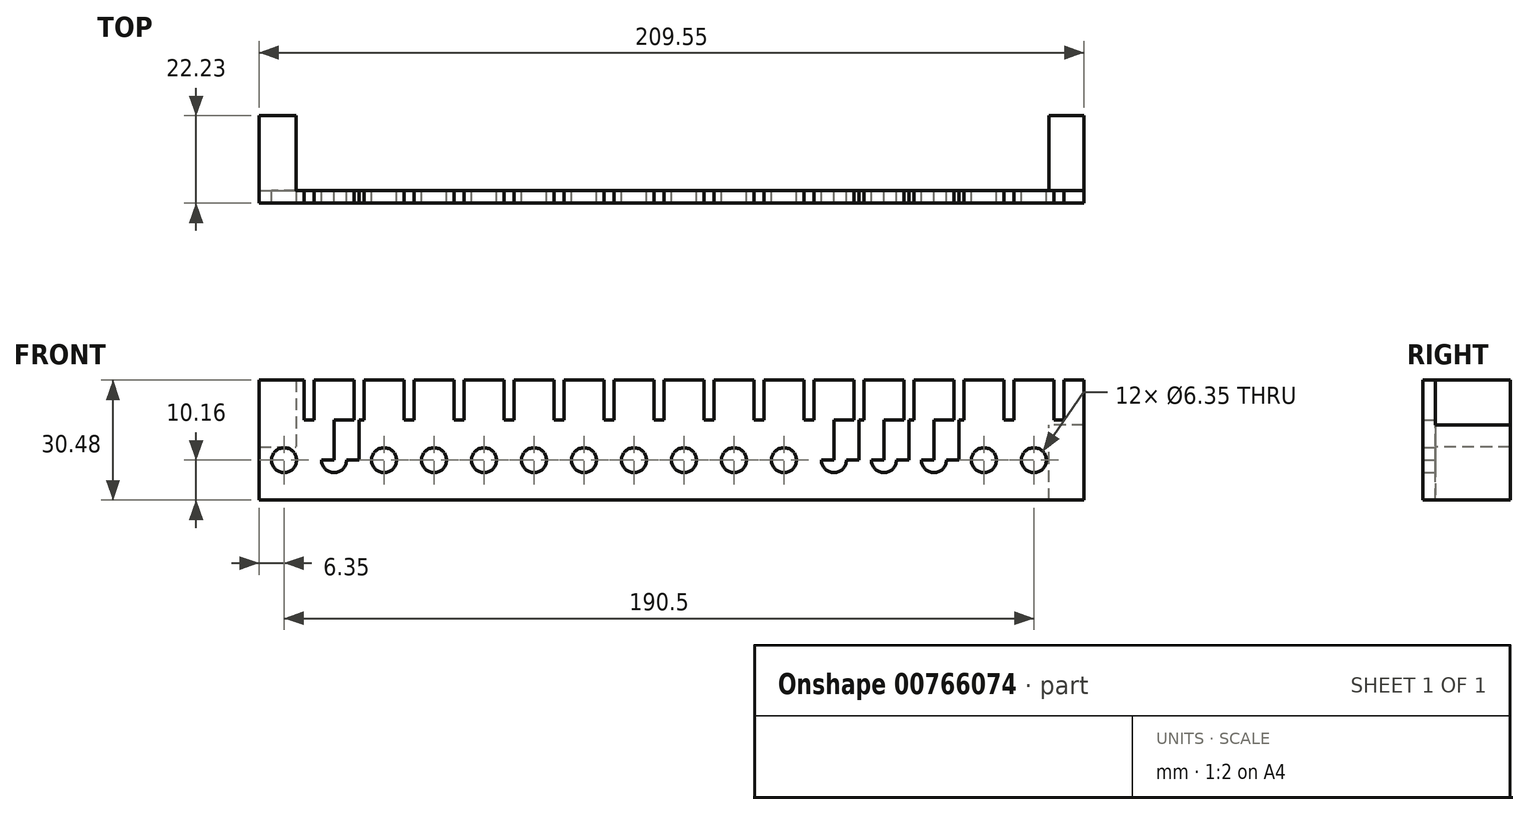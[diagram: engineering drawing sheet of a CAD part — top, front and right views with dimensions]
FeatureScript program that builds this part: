
annotation { "Feature Type Name" : "Feature", "Feature Type Description" : "" }
export const myFeature = defineFeature(function(context is Context, id is Id, definition is map)
    precondition{}
    {
        {
            var Q0;
            Q0=qCreatedBy(makeId("Front.planeOp"),FACE);
            var sketch = newSketch(context, id + "F0", { "sketchPlane" : qUnion([Q0])});
            skLineSegment(sketch, "E0.bottom", {"start": v(-95.25, 15.24) * mm, "end": v(95.25, 15.24) * mm});
            skLineSegment(sketch, "E0.top", {"start": v(-95.25, -15.24) * mm, "end": v(95.25, -15.24) * mm});
            skLineSegment(sketch, "E0.left", {"start": v(-95.25, 15.24) * mm, "end": v(-95.25, -15.24) * mm});
            skLineSegment(sketch, "E0.right", {"start": v(95.25, 15.24) * mm, "end": v(95.25, -15.24) * mm});
            skPoint(sketch, "E0.middle", {"position": v(0, 0) * mm});
            skLineSegment(sketch, "E1", {"start": v(-95.25, -5.08) * mm, "end": v(95.25, -5.08) * mm});
            skLineSegment(sketch, "E2", {"start": v(-95.25, 5.08) * mm, "end": v(95.25, 5.08) * mm});
            skLineSegment(sketch, "E3", {"start": v(-88.9, 15.24) * mm, "end": v(-88.9, -15.24) * mm});
            skLineSegment(sketch, "E4", {"start": v(-76.2, 15.24) * mm, "end": v(-76.2, -15.24) * mm});
            skLineSegment(sketch, "E5", {"start": v(-82.55, 15.24) * mm, "end": v(-82.55, -15.24) * mm});
            skLineSegment(sketch, "E6", {"start": v(-69.85, 15.24) * mm, "end": v(-69.85, -15.24) * mm});
            skLineSegment(sketch, "E7.bottom", {"start": v(-81.28, 5.08) * mm, "end": v(-83.82, 5.08) * mm});
            skLineSegment(sketch, "E7.top", {"start": v(-81.28, 25.4) * mm, "end": v(-83.82, 25.4) * mm});
            skLineSegment(sketch, "E7.left", {"start": v(-81.28, 5.08) * mm, "end": v(-81.28, 25.4) * mm});
            skLineSegment(sketch, "E7.right", {"start": v(-83.82, 5.08) * mm, "end": v(-83.82, 25.4) * mm});
            skPoint(sketch, "E7.middle", {"position": v(-82.55, 15.24) * mm});
            skLineSegment(sketch, "E8.bottom", {"start": v(-68.58, 5.08) * mm, "end": v(-71.12, 5.08) * mm});
            skLineSegment(sketch, "E8.top", {"start": v(-68.58, 25.4) * mm, "end": v(-71.12, 25.4) * mm});
            skLineSegment(sketch, "E8.left", {"start": v(-68.58, 5.08) * mm, "end": v(-68.58, 25.4) * mm});
            skLineSegment(sketch, "E8.right", {"start": v(-71.12, 5.08) * mm, "end": v(-71.12, 25.4) * mm});
            skPoint(sketch, "E8.middle", {"position": v(-69.85, 15.24) * mm});
            skCircle(sketch, "E9", {"center": v(-88.9, -5.08) * mm, "radius": 3.18 * mm});
            skCircle(sketch, "E10", {"center": v(-76.2, -5.08) * mm, "radius": 3.18 * mm});
            skLineSegment(sketch, "E11", {"start": v(-63.5, 15.24) * mm, "end": v(-63.5, -15.24) * mm});
            skLineSegment(sketch, "E12", {"start": v(-50.8, 15.24) * mm, "end": v(-50.8, -15.24) * mm});
            skLineSegment(sketch, "E13", {"start": v(-57.15, 15.24) * mm, "end": v(-57.15, -15.24) * mm});
            skLineSegment(sketch, "E14", {"start": v(-44.45, 15.24) * mm, "end": v(-44.45, -15.24) * mm});
            skLineSegment(sketch, "E15.bottom", {"start": v(-55.88, 5.08) * mm, "end": v(-58.42, 5.08) * mm});
            skLineSegment(sketch, "E15.top", {"start": v(-55.88, 25.4) * mm, "end": v(-58.42, 25.4) * mm});
            skLineSegment(sketch, "E15.left", {"start": v(-55.88, 5.08) * mm, "end": v(-55.88, 25.4) * mm});
            skLineSegment(sketch, "E15.right", {"start": v(-58.42, 5.08) * mm, "end": v(-58.42, 25.4) * mm});
            skPoint(sketch, "E15.middle", {"position": v(-57.15, 15.24) * mm});
            skLineSegment(sketch, "E16.bottom", {"start": v(-43.18, 5.08) * mm, "end": v(-45.72, 5.08) * mm});
            skLineSegment(sketch, "E16.top", {"start": v(-43.18, 25.4) * mm, "end": v(-45.72, 25.4) * mm});
            skLineSegment(sketch, "E16.left", {"start": v(-43.18, 5.08) * mm, "end": v(-43.18, 25.4) * mm});
            skLineSegment(sketch, "E16.right", {"start": v(-45.72, 5.08) * mm, "end": v(-45.72, 25.4) * mm});
            skPoint(sketch, "E16.middle", {"position": v(-44.45, 15.24) * mm});
            skCircle(sketch, "E17", {"center": v(-63.5, -5.08) * mm, "radius": 3.18 * mm});
            skCircle(sketch, "E18", {"center": v(-50.8, -5.08) * mm, "radius": 3.18 * mm});
            skLineSegment(sketch, "E19", {"start": v(-38.1, 15.24) * mm, "end": v(-38.1, -15.24) * mm});
            skLineSegment(sketch, "E20", {"start": v(-25.4, 15.24) * mm, "end": v(-25.4, -15.24) * mm});
            skLineSegment(sketch, "E21", {"start": v(-31.75, 15.24) * mm, "end": v(-31.75, -15.24) * mm});
            skLineSegment(sketch, "E22", {"start": v(-19.05, 15.24) * mm, "end": v(-19.05, -15.24) * mm});
            skLineSegment(sketch, "E23.bottom", {"start": v(-30.48, 5.08) * mm, "end": v(-33.02, 5.08) * mm});
            skLineSegment(sketch, "E23.top", {"start": v(-30.48, 25.4) * mm, "end": v(-33.02, 25.4) * mm});
            skLineSegment(sketch, "E23.left", {"start": v(-30.48, 5.08) * mm, "end": v(-30.48, 25.4) * mm});
            skLineSegment(sketch, "E23.right", {"start": v(-33.02, 5.08) * mm, "end": v(-33.02, 25.4) * mm});
            skPoint(sketch, "E23.middle", {"position": v(-31.75, 15.24) * mm});
            skLineSegment(sketch, "E24.bottom", {"start": v(-17.78, 5.08) * mm, "end": v(-20.32, 5.08) * mm});
            skLineSegment(sketch, "E24.top", {"start": v(-17.78, 25.4) * mm, "end": v(-20.32, 25.4) * mm});
            skLineSegment(sketch, "E24.left", {"start": v(-17.78, 5.08) * mm, "end": v(-17.78, 25.4) * mm});
            skLineSegment(sketch, "E24.right", {"start": v(-20.32, 5.08) * mm, "end": v(-20.32, 25.4) * mm});
            skPoint(sketch, "E24.middle", {"position": v(-19.05, 15.24) * mm});
            skCircle(sketch, "E25", {"center": v(-38.1, -5.08) * mm, "radius": 3.18 * mm});
            skCircle(sketch, "E26", {"center": v(-25.4, -5.08) * mm, "radius": 3.18 * mm});
            skLineSegment(sketch, "E27", {"start": v(-12.7, 15.24) * mm, "end": v(-12.7, -15.24) * mm});
            skLineSegment(sketch, "E28", {"start": v(0, 15.24) * mm, "end": v(0, -15.24) * mm});
            skLineSegment(sketch, "E29", {"start": v(-6.35, 15.24) * mm, "end": v(-6.35, -15.24) * mm});
            skLineSegment(sketch, "E30", {"start": v(6.35, 15.24) * mm, "end": v(6.35, -15.24) * mm});
            skLineSegment(sketch, "E31.bottom", {"start": v(-5.08, 5.08) * mm, "end": v(-7.62, 5.08) * mm});
            skLineSegment(sketch, "E31.top", {"start": v(-5.08, 25.4) * mm, "end": v(-7.62, 25.4) * mm});
            skLineSegment(sketch, "E31.left", {"start": v(-5.08, 5.08) * mm, "end": v(-5.08, 25.4) * mm});
            skLineSegment(sketch, "E31.right", {"start": v(-7.62, 5.08) * mm, "end": v(-7.62, 25.4) * mm});
            skPoint(sketch, "E31.middle", {"position": v(-6.35, 15.24) * mm});
            skLineSegment(sketch, "E32.bottom", {"start": v(7.62, 5.08) * mm, "end": v(5.08, 5.08) * mm});
            skLineSegment(sketch, "E32.top", {"start": v(7.62, 25.4) * mm, "end": v(5.08, 25.4) * mm});
            skLineSegment(sketch, "E32.left", {"start": v(7.62, 5.08) * mm, "end": v(7.62, 25.4) * mm});
            skLineSegment(sketch, "E32.right", {"start": v(5.08, 5.08) * mm, "end": v(5.08, 25.4) * mm});
            skPoint(sketch, "E32.middle", {"position": v(6.35, 15.24) * mm});
            skCircle(sketch, "E33", {"center": v(-12.7, -5.08) * mm, "radius": 3.18 * mm});
            skCircle(sketch, "E34", {"center": v(0, -5.08) * mm, "radius": 3.18 * mm});
            skLineSegment(sketch, "E35", {"start": v(12.7, 15.24) * mm, "end": v(12.7, -15.24) * mm});
            skLineSegment(sketch, "E36", {"start": v(25.4, 15.24) * mm, "end": v(25.4, -15.24) * mm});
            skLineSegment(sketch, "E37", {"start": v(19.05, 15.24) * mm, "end": v(19.05, -15.24) * mm});
            skLineSegment(sketch, "E38", {"start": v(31.75, 15.24) * mm, "end": v(31.75, -15.24) * mm});
            skLineSegment(sketch, "E39.bottom", {"start": v(20.32, 5.08) * mm, "end": v(17.78, 5.08) * mm});
            skLineSegment(sketch, "E39.top", {"start": v(20.32, 25.4) * mm, "end": v(17.78, 25.4) * mm});
            skLineSegment(sketch, "E39.left", {"start": v(20.32, 5.08) * mm, "end": v(20.32, 25.4) * mm});
            skLineSegment(sketch, "E39.right", {"start": v(17.78, 5.08) * mm, "end": v(17.78, 25.4) * mm});
            skPoint(sketch, "E39.middle", {"position": v(19.05, 15.24) * mm});
            skLineSegment(sketch, "E40.bottom", {"start": v(33.02, 5.08) * mm, "end": v(30.48, 5.08) * mm});
            skLineSegment(sketch, "E40.top", {"start": v(33.02, 25.4) * mm, "end": v(30.48, 25.4) * mm});
            skLineSegment(sketch, "E40.left", {"start": v(33.02, 5.08) * mm, "end": v(33.02, 25.4) * mm});
            skLineSegment(sketch, "E40.right", {"start": v(30.48, 5.08) * mm, "end": v(30.48, 25.4) * mm});
            skPoint(sketch, "E40.middle", {"position": v(31.75, 15.24) * mm});
            skCircle(sketch, "E41", {"center": v(12.7, -5.08) * mm, "radius": 3.18 * mm});
            skCircle(sketch, "E42", {"center": v(25.4, -5.08) * mm, "radius": 3.18 * mm});
            skLineSegment(sketch, "E43", {"start": v(38.1, 15.24) * mm, "end": v(38.1, -15.24) * mm});
            skLineSegment(sketch, "E44", {"start": v(50.8, 15.24) * mm, "end": v(50.8, -15.24) * mm});
            skLineSegment(sketch, "E45", {"start": v(44.45, 15.24) * mm, "end": v(44.45, -15.24) * mm});
            skLineSegment(sketch, "E46", {"start": v(57.15, 15.24) * mm, "end": v(57.15, -15.24) * mm});
            skLineSegment(sketch, "E47.bottom", {"start": v(45.72, 5.08) * mm, "end": v(43.18, 5.08) * mm});
            skLineSegment(sketch, "E47.top", {"start": v(45.72, 25.4) * mm, "end": v(43.18, 25.4) * mm});
            skLineSegment(sketch, "E47.left", {"start": v(45.72, 5.08) * mm, "end": v(45.72, 25.4) * mm});
            skLineSegment(sketch, "E47.right", {"start": v(43.18, 5.08) * mm, "end": v(43.18, 25.4) * mm});
            skPoint(sketch, "E47.middle", {"position": v(44.45, 15.24) * mm});
            skLineSegment(sketch, "E48.bottom", {"start": v(58.42, 5.08) * mm, "end": v(55.88, 5.08) * mm});
            skLineSegment(sketch, "E48.top", {"start": v(58.42, 25.4) * mm, "end": v(55.88, 25.4) * mm});
            skLineSegment(sketch, "E48.left", {"start": v(58.42, 5.08) * mm, "end": v(58.42, 25.4) * mm});
            skLineSegment(sketch, "E48.right", {"start": v(55.88, 5.08) * mm, "end": v(55.88, 25.4) * mm});
            skPoint(sketch, "E48.middle", {"position": v(57.15, 15.24) * mm});
            skCircle(sketch, "E49", {"center": v(38.1, -5.08) * mm, "radius": 3.18 * mm});
            skCircle(sketch, "E50", {"center": v(50.8, -5.08) * mm, "radius": 3.18 * mm});
            skLineSegment(sketch, "E51", {"start": v(63.5, 15.24) * mm, "end": v(63.5, -15.24) * mm});
            skLineSegment(sketch, "E52", {"start": v(76.2, 15.24) * mm, "end": v(76.2, -15.24) * mm});
            skLineSegment(sketch, "E53", {"start": v(69.85, 15.24) * mm, "end": v(69.85, -15.24) * mm});
            skLineSegment(sketch, "E54", {"start": v(82.55, 15.24) * mm, "end": v(82.55, -15.24) * mm});
            skLineSegment(sketch, "E55.bottom", {"start": v(71.12, 5.08) * mm, "end": v(68.58, 5.08) * mm});
            skLineSegment(sketch, "E55.top", {"start": v(71.12, 25.4) * mm, "end": v(68.58, 25.4) * mm});
            skLineSegment(sketch, "E55.left", {"start": v(71.12, 5.08) * mm, "end": v(71.12, 25.4) * mm});
            skLineSegment(sketch, "E55.right", {"start": v(68.58, 5.08) * mm, "end": v(68.58, 25.4) * mm});
            skPoint(sketch, "E55.middle", {"position": v(69.85, 15.24) * mm});
            skLineSegment(sketch, "E56.bottom", {"start": v(83.82, 5.08) * mm, "end": v(81.28, 5.08) * mm});
            skLineSegment(sketch, "E56.top", {"start": v(83.82, 25.4) * mm, "end": v(81.28, 25.4) * mm});
            skLineSegment(sketch, "E56.left", {"start": v(83.82, 5.08) * mm, "end": v(83.82, 25.4) * mm});
            skLineSegment(sketch, "E56.right", {"start": v(81.28, 5.08) * mm, "end": v(81.28, 25.4) * mm});
            skPoint(sketch, "E56.middle", {"position": v(82.55, 15.24) * mm});
            skCircle(sketch, "E57", {"center": v(63.5, -5.08) * mm, "radius": 3.18 * mm});
            skCircle(sketch, "E58", {"center": v(76.2, -5.08) * mm, "radius": 3.18 * mm});
            skLineSegment(sketch, "E59", {"start": v(88.9, 15.24) * mm, "end": v(88.9, -15.24) * mm});
            skLineSegment(sketch, "E60", {"start": v(101.6, 15.24) * mm, "end": v(101.6, -15.24) * mm});
            skLineSegment(sketch, "E61", {"start": v(107.95, 15.24) * mm, "end": v(107.95, -15.24) * mm});
            skLineSegment(sketch, "E62.bottom", {"start": v(96.52, 5.08) * mm, "end": v(93.98, 5.08) * mm});
            skLineSegment(sketch, "E62.top", {"start": v(96.52, 25.4) * mm, "end": v(93.98, 25.4) * mm});
            skLineSegment(sketch, "E62.left", {"start": v(96.52, 5.08) * mm, "end": v(96.52, 25.4) * mm});
            skLineSegment(sketch, "E62.right", {"start": v(93.98, 5.08) * mm, "end": v(93.98, 25.4) * mm});
            skPoint(sketch, "E62.middle", {"position": v(95.25, 15.24) * mm});
            skLineSegment(sketch, "E63.bottom", {"start": v(109.22, 5.08) * mm, "end": v(106.68, 5.08) * mm});
            skLineSegment(sketch, "E63.top", {"start": v(109.22, 25.4) * mm, "end": v(106.68, 25.4) * mm});
            skLineSegment(sketch, "E63.left", {"start": v(109.22, 5.08) * mm, "end": v(109.22, 25.4) * mm});
            skLineSegment(sketch, "E63.right", {"start": v(106.68, 5.08) * mm, "end": v(106.68, 25.4) * mm});
            skPoint(sketch, "E63.middle", {"position": v(107.95, 15.24) * mm});
            skCircle(sketch, "E64", {"center": v(88.9, -5.08) * mm, "radius": 3.18 * mm});
            skCircle(sketch, "E65", {"center": v(101.6, -5.08) * mm, "radius": 3.18 * mm});
            skLineSegment(sketch, "E66.bottom", {"start": v(95.25, 15.24) * mm, "end": v(114.3, 15.24) * mm});
            skLineSegment(sketch, "E66.top", {"start": v(95.25, -15.24) * mm, "end": v(114.3, -15.24) * mm});
            skLineSegment(sketch, "E66.right", {"start": v(114.3, 15.24) * mm, "end": v(114.3, -15.24) * mm});
            skSolve(sketch);
        }
        {
            var Q0;
            {var subQ0=sQuery(id+"F0.wireOp",EDGE,"E20");var subQ1=sQuery(id+"F0.wireOp",EDGE,"E0.bottom");var subQ2=makeQuery(id+"F0.imprint","INTERSECT",VERTEX,{"derivedFrom":[subQ1,subQ0]});Q0=makeQuery(id+"F0.imprint","IMPRINT",FACE,{"disambiguationData":[TD([[makeQuery(id+"F0.imprint","IMPRINT",EDGE,{"disambiguationData":[TD([[subQ2,-1.0]])],"derivedFrom":subQ1}),-1.0]])]});}
            var Q1;
            {var subQ0=sQuery(id+"F0.wireOp",EDGE,"E19");var subQ1=sQuery(id+"F0.wireOp",EDGE,"E0.bottom");var subQ2=makeQuery(id+"F0.imprint","INTERSECT",VERTEX,{"derivedFrom":[subQ1,subQ0]});Q1=makeQuery(id+"F0.imprint","IMPRINT",FACE,{"disambiguationData":[TD([[makeQuery(id+"F0.imprint","IMPRINT",EDGE,{"disambiguationData":[TD([[subQ2,-1.0]])],"derivedFrom":subQ1}),-1.0]])]});}
            var Q2;
            {var subQ1=sQuery(id+"F0.wireOp",EDGE,"E0.top");var subQ5=sQuery(id+"F0.wireOp",EDGE,"E38");var subQ6=makeQuery(id+"F0.imprint","INTERSECT",VERTEX,{"derivedFrom":[subQ1,subQ5]});Q2=makeQuery(id+"F0.imprint","IMPRINT",FACE,{"disambiguationData":[TD([[makeQuery(id+"F0.imprint","IMPRINT",EDGE,{"disambiguationData":[TD([[subQ6,-1.0]])],"derivedFrom":subQ1}),1.0]])]});}
            var Q3;
            {var subQ7=sQuery(id+"F0.wireOp",EDGE,"E50");var subQ9=sQuery(id+"F0.wireOp",EDGE,"E1");var subQ10=makeQuery(id+"F0.imprint","INTERSECT",VERTEX,{"disambiguationData":[OD(1.0)],"derivedFrom":[subQ9,subQ7]});Q3=makeQuery(id+"F0.imprint","IMPRINT",FACE,{"disambiguationData":[TD([[makeQuery(id+"F0.imprint","IMPRINT",EDGE,{"disambiguationData":[TD([[subQ10,-1.0]])],"derivedFrom":subQ9}),1.0]])]});}
            var Q4;
            {var subQ0=sQuery(id+"F0.wireOp",EDGE,"E51");var subQ1=sQuery(id+"F0.wireOp",EDGE,"E0.bottom");var subQ2=makeQuery(id+"F0.imprint","INTERSECT",VERTEX,{"derivedFrom":[subQ1,subQ0]});Q4=makeQuery(id+"F0.imprint","IMPRINT",FACE,{"disambiguationData":[TD([[makeQuery(id+"F0.imprint","IMPRINT",EDGE,{"disambiguationData":[TD([[subQ2,-1.0]])],"derivedFrom":subQ1}),-1.0]])]});}
            var Q5;
            {var subQ1=sQuery(id+"F0.wireOp",EDGE,"E1");var subQ8=sQuery(id+"F0.wireOp",EDGE,"E9");var subQ10=makeQuery(id+"F0.imprint","INTERSECT",VERTEX,{"disambiguationData":[OD(1.0)],"derivedFrom":[subQ1,subQ8]});Q5=makeQuery(id+"F0.imprint","IMPRINT",FACE,{"disambiguationData":[TD([[makeQuery(id+"F0.imprint","IMPRINT",EDGE,{"disambiguationData":[TD([[subQ10,-1.0]])],"derivedFrom":subQ1}),1.0]])]});}
            var Q6;
            {var subQ0=sQuery(id+"F0.wireOp",EDGE,"E13");var subQ1=sQuery(id+"F0.wireOp",EDGE,"E1");var subQ2=makeQuery(id+"F0.imprint","INTERSECT",VERTEX,{"derivedFrom":[subQ1,subQ0]});Q6=makeQuery(id+"F0.imprint","IMPRINT",FACE,{"disambiguationData":[TD([[makeQuery(id+"F0.imprint","IMPRINT",EDGE,{"disambiguationData":[TD([[subQ2,-1.0]])],"derivedFrom":subQ1}),1.0]])]});}
            var Q7;
            {var subQ0=sQuery(id+"F0.wireOp",EDGE,"E14");var subQ6=sQuery(id+"F0.wireOp",EDGE,"E0.top");var subQ9=makeQuery(id+"F0.imprint","INTERSECT",VERTEX,{"derivedFrom":[subQ6,subQ0]});Q7=makeQuery(id+"F0.imprint","IMPRINT",FACE,{"disambiguationData":[TD([[makeQuery(id+"F0.imprint","IMPRINT",EDGE,{"disambiguationData":[TD([[subQ9,-1.0]])],"derivedFrom":subQ6}),1.0]])]});}
            var Q8;
            {var subQ7=sQuery(id+"F0.wireOp",EDGE,"E18");var subQ9=sQuery(id+"F0.wireOp",EDGE,"E1");var subQ10=makeQuery(id+"F0.imprint","INTERSECT",VERTEX,{"disambiguationData":[OD(1.0)],"derivedFrom":[subQ9,subQ7]});Q8=makeQuery(id+"F0.imprint","IMPRINT",FACE,{"disambiguationData":[TD([[makeQuery(id+"F0.imprint","IMPRINT",EDGE,{"disambiguationData":[TD([[subQ10,-1.0]])],"derivedFrom":subQ9}),1.0]])]});}
            var Q9;
            {var subQ1=sQuery(id+"F0.wireOp",EDGE,"E0.top");var subQ7=sQuery(id+"F0.wireOp",EDGE,"E11");var subQ8=makeQuery(id+"F0.imprint","INTERSECT",VERTEX,{"derivedFrom":[subQ1,subQ7]});Q9=makeQuery(id+"F0.imprint","IMPRINT",FACE,{"disambiguationData":[TD([[makeQuery(id+"F0.imprint","IMPRINT",EDGE,{"disambiguationData":[TD([[subQ8,-1.0]])],"derivedFrom":subQ1}),1.0]])]});}
            var Q10;
            {var subQ3=sQuery(id+"F0.wireOp",EDGE,"E4");var subQ5=sQuery(id+"F0.wireOp",EDGE,"E0.top");var subQ6=makeQuery(id+"F0.imprint","INTERSECT",VERTEX,{"derivedFrom":[subQ5,subQ3]});Q10=makeQuery(id+"F0.imprint","IMPRINT",FACE,{"disambiguationData":[TD([[makeQuery(id+"F0.imprint","IMPRINT",EDGE,{"disambiguationData":[TD([[subQ6,-1.0]])],"derivedFrom":subQ5}),1.0]])]});}
            var Q11;
            {var subQ7=sQuery(id+"F0.wireOp",EDGE,"E34");var subQ9=sQuery(id+"F0.wireOp",EDGE,"E1");var subQ10=makeQuery(id+"F0.imprint","INTERSECT",VERTEX,{"disambiguationData":[OD(1.0)],"derivedFrom":[subQ9,subQ7]});Q11=makeQuery(id+"F0.imprint","IMPRINT",FACE,{"disambiguationData":[TD([[makeQuery(id+"F0.imprint","IMPRINT",EDGE,{"disambiguationData":[TD([[subQ10,-1.0]])],"derivedFrom":subQ9}),1.0]])]});}
            var Q12;
            {var subQ0=sQuery(id+"F0.wireOp",EDGE,"E52");var subQ1=sQuery(id+"F0.wireOp",EDGE,"E0.bottom");var subQ2=makeQuery(id+"F0.imprint","INTERSECT",VERTEX,{"derivedFrom":[subQ1,subQ0]});Q12=makeQuery(id+"F0.imprint","IMPRINT",FACE,{"disambiguationData":[TD([[makeQuery(id+"F0.imprint","IMPRINT",EDGE,{"disambiguationData":[TD([[subQ2,-1.0]])],"derivedFrom":subQ1}),-1.0]])]});}
            var Q13;
            {var subQ1=sQuery(id+"F0.wireOp",EDGE,"E0.top");var subQ5=sQuery(id+"F0.wireOp",EDGE,"E6");var subQ6=makeQuery(id+"F0.imprint","INTERSECT",VERTEX,{"derivedFrom":[subQ1,subQ5]});Q13=makeQuery(id+"F0.imprint","IMPRINT",FACE,{"disambiguationData":[TD([[makeQuery(id+"F0.imprint","IMPRINT",EDGE,{"disambiguationData":[TD([[subQ6,-1.0]])],"derivedFrom":subQ1}),1.0]])]});}
            var Q14;
            {var subQ0=sQuery(id+"F0.wireOp",EDGE,"E28");var subQ1=sQuery(id+"F0.wireOp",EDGE,"E0.bottom");var subQ2=makeQuery(id+"F0.imprint","INTERSECT",VERTEX,{"derivedFrom":[subQ1,subQ0]});Q14=makeQuery(id+"F0.imprint","IMPRINT",FACE,{"disambiguationData":[TD([[makeQuery(id+"F0.imprint","IMPRINT",EDGE,{"disambiguationData":[TD([[subQ2,-1.0]])],"derivedFrom":subQ1}),-1.0]])]});}
            var Q15;
            {var subQ1=sQuery(id+"F0.wireOp",EDGE,"E0.top");var subQ5=sQuery(id+"F0.wireOp",EDGE,"E43");var subQ6=makeQuery(id+"F0.imprint","INTERSECT",VERTEX,{"derivedFrom":[subQ1,subQ5]});Q15=makeQuery(id+"F0.imprint","IMPRINT",FACE,{"disambiguationData":[TD([[makeQuery(id+"F0.imprint","IMPRINT",EDGE,{"disambiguationData":[TD([[subQ6,-1.0]])],"derivedFrom":subQ1}),1.0]])]});}
            var Q16;
            {var subQ0=sQuery(id+"F0.wireOp",EDGE,"E35");var subQ1=sQuery(id+"F0.wireOp",EDGE,"E0.bottom");var subQ2=makeQuery(id+"F0.imprint","INTERSECT",VERTEX,{"derivedFrom":[subQ1,subQ0]});Q16=makeQuery(id+"F0.imprint","IMPRINT",FACE,{"disambiguationData":[TD([[makeQuery(id+"F0.imprint","IMPRINT",EDGE,{"disambiguationData":[TD([[subQ2,1.0]])],"derivedFrom":subQ1}),-1.0]])]});}
            var Q17;
            {var subQ0=sQuery(id+"F0.wireOp",EDGE,"E36");var subQ1=sQuery(id+"F0.wireOp",EDGE,"E0.bottom");var subQ2=makeQuery(id+"F0.imprint","INTERSECT",VERTEX,{"derivedFrom":[subQ1,subQ0]});Q17=makeQuery(id+"F0.imprint","IMPRINT",FACE,{"disambiguationData":[TD([[makeQuery(id+"F0.imprint","IMPRINT",EDGE,{"disambiguationData":[TD([[subQ2,1.0]])],"derivedFrom":subQ1}),-1.0]])]});}
            var Q18;
            {var subQ0=sQuery(id+"F0.wireOp",EDGE,"E35");var subQ1=sQuery(id+"F0.wireOp",EDGE,"E0.top");var subQ2=makeQuery(id+"F0.imprint","INTERSECT",VERTEX,{"derivedFrom":[subQ1,subQ0]});Q18=makeQuery(id+"F0.imprint","IMPRINT",FACE,{"disambiguationData":[TD([[makeQuery(id+"F0.imprint","IMPRINT",EDGE,{"disambiguationData":[TD([[subQ2,-1.0]])],"derivedFrom":subQ1}),1.0]])]});}
            var Q19;
            {var subQ5=sQuery(id+"F0.wireOp",EDGE,"E36");var subQ7=sQuery(id+"F0.wireOp",EDGE,"E0.top");var subQ8=makeQuery(id+"F0.imprint","INTERSECT",VERTEX,{"derivedFrom":[subQ7,subQ5]});Q19=makeQuery(id+"F0.imprint","IMPRINT",FACE,{"disambiguationData":[TD([[makeQuery(id+"F0.imprint","IMPRINT",EDGE,{"disambiguationData":[TD([[subQ8,-1.0]])],"derivedFrom":subQ7}),1.0]])]});}
            var Q20;
            {var subQ1=sQuery(id+"F0.wireOp",EDGE,"E1");var subQ9=sQuery(id+"F0.wireOp",EDGE,"E41");var subQ11=makeQuery(id+"F0.imprint","INTERSECT",VERTEX,{"disambiguationData":[OD(1.0)],"derivedFrom":[subQ1,subQ9]});Q20=makeQuery(id+"F0.imprint","IMPRINT",FACE,{"disambiguationData":[TD([[makeQuery(id+"F0.imprint","IMPRINT",EDGE,{"disambiguationData":[TD([[subQ11,-1.0]])],"derivedFrom":subQ1}),1.0]])]});}
            var Q21;
            {var subQ1=sQuery(id+"F0.wireOp",EDGE,"E1");var subQ8=sQuery(id+"F0.wireOp",EDGE,"E17");var subQ11=makeQuery(id+"F0.imprint","INTERSECT",VERTEX,{"disambiguationData":[OD(1.0)],"derivedFrom":[subQ1,subQ8]});Q21=makeQuery(id+"F0.imprint","IMPRINT",FACE,{"disambiguationData":[TD([[makeQuery(id+"F0.imprint","IMPRINT",EDGE,{"disambiguationData":[TD([[subQ11,-1.0]])],"derivedFrom":subQ1}),1.0]])]});}
            var Q22;
            {var subQ7=sQuery(id+"F0.wireOp",EDGE,"E10");var subQ9=sQuery(id+"F0.wireOp",EDGE,"E1");var subQ10=makeQuery(id+"F0.imprint","INTERSECT",VERTEX,{"disambiguationData":[OD(1.0)],"derivedFrom":[subQ9,subQ7]});Q22=makeQuery(id+"F0.imprint","IMPRINT",FACE,{"disambiguationData":[TD([[makeQuery(id+"F0.imprint","IMPRINT",EDGE,{"disambiguationData":[TD([[subQ10,-1.0]])],"derivedFrom":subQ9}),1.0]])]});}
            var Q23;
            {var subQ0=sQuery(id+"F0.wireOp",EDGE,"E28");var subQ1=sQuery(id+"F0.wireOp",EDGE,"E0.bottom");var subQ2=makeQuery(id+"F0.imprint","INTERSECT",VERTEX,{"derivedFrom":[subQ1,subQ0]});Q23=makeQuery(id+"F0.imprint","IMPRINT",FACE,{"disambiguationData":[TD([[makeQuery(id+"F0.imprint","IMPRINT",EDGE,{"disambiguationData":[TD([[subQ2,1.0]])],"derivedFrom":subQ1}),-1.0]])]});}
            var Q24;
            {var subQ0=sQuery(id+"F0.wireOp",EDGE,"E59");var subQ1=sQuery(id+"F0.wireOp",EDGE,"E0.bottom");var subQ2=makeQuery(id+"F0.imprint","INTERSECT",VERTEX,{"derivedFrom":[subQ1,subQ0]});Q24=makeQuery(id+"F0.imprint","IMPRINT",FACE,{"disambiguationData":[TD([[makeQuery(id+"F0.imprint","IMPRINT",EDGE,{"disambiguationData":[TD([[subQ2,-1.0]])],"derivedFrom":subQ1}),-1.0]])]});}
            var Q25;
            {var subQ7=sQuery(id+"F0.wireOp",EDGE,"E42");var subQ9=sQuery(id+"F0.wireOp",EDGE,"E1");var subQ10=makeQuery(id+"F0.imprint","INTERSECT",VERTEX,{"disambiguationData":[OD(1.0)],"derivedFrom":[subQ9,subQ7]});Q25=makeQuery(id+"F0.imprint","IMPRINT",FACE,{"disambiguationData":[TD([[makeQuery(id+"F0.imprint","IMPRINT",EDGE,{"disambiguationData":[TD([[subQ10,-1.0]])],"derivedFrom":subQ9}),1.0]])]});}
            var Q26;
            {var subQ1=sQuery(id+"F0.wireOp",EDGE,"E0.top");var subQ5=sQuery(id+"F0.wireOp",EDGE,"E46");var subQ6=makeQuery(id+"F0.imprint","INTERSECT",VERTEX,{"derivedFrom":[subQ1,subQ5]});Q26=makeQuery(id+"F0.imprint","IMPRINT",FACE,{"disambiguationData":[TD([[makeQuery(id+"F0.imprint","IMPRINT",EDGE,{"disambiguationData":[TD([[subQ6,-1.0]])],"derivedFrom":subQ1}),1.0]])]});}
            var Q27;
            {var subQ0=sQuery(id+"F0.wireOp",EDGE,"E4");var subQ1=sQuery(id+"F0.wireOp",EDGE,"E0.bottom");var subQ2=makeQuery(id+"F0.imprint","INTERSECT",VERTEX,{"derivedFrom":[subQ1,subQ0]});Q27=makeQuery(id+"F0.imprint","IMPRINT",FACE,{"disambiguationData":[TD([[makeQuery(id+"F0.imprint","IMPRINT",EDGE,{"disambiguationData":[TD([[subQ2,1.0]])],"derivedFrom":subQ1}),-1.0]])]});}
            var Q28;
            {var subQ3=sQuery(id+"F0.wireOp",EDGE,"E44");var subQ5=sQuery(id+"F0.wireOp",EDGE,"E0.top");var subQ6=makeQuery(id+"F0.imprint","INTERSECT",VERTEX,{"derivedFrom":[subQ5,subQ3]});Q28=makeQuery(id+"F0.imprint","IMPRINT",FACE,{"disambiguationData":[TD([[makeQuery(id+"F0.imprint","IMPRINT",EDGE,{"disambiguationData":[TD([[subQ6,-1.0]])],"derivedFrom":subQ5}),1.0]])]});}
            var Q29;
            {var subQ0=sQuery(id+"F0.wireOp",EDGE,"E14");var subQ1=sQuery(id+"F0.wireOp",EDGE,"E1");var subQ2=makeQuery(id+"F0.imprint","INTERSECT",VERTEX,{"derivedFrom":[subQ1,subQ0]});Q29=makeQuery(id+"F0.imprint","IMPRINT",FACE,{"disambiguationData":[TD([[makeQuery(id+"F0.imprint","IMPRINT",EDGE,{"disambiguationData":[TD([[subQ2,-1.0]])],"derivedFrom":subQ1}),1.0]])]});}
            var Q30;
            {var subQ0=sQuery(id+"F0.wireOp",EDGE,"E46");var subQ1=sQuery(id+"F0.wireOp",EDGE,"E1");var subQ2=makeQuery(id+"F0.imprint","INTERSECT",VERTEX,{"derivedFrom":[subQ1,subQ0]});Q30=makeQuery(id+"F0.imprint","IMPRINT",FACE,{"disambiguationData":[TD([[makeQuery(id+"F0.imprint","IMPRINT",EDGE,{"disambiguationData":[TD([[subQ2,-1.0]])],"derivedFrom":subQ1}),1.0]])]});}
            var Q31;
            {var subQ1=sQuery(id+"F0.wireOp",EDGE,"E0.left");var subQ5=sQuery(id+"F0.wireOp",EDGE,"E0.top");var subQ6=makeQuery(id+"F0.imprint","INTERSECT",VERTEX,{"derivedFrom":[subQ5,subQ1]});Q31=makeQuery(id+"F0.imprint","IMPRINT",FACE,{"disambiguationData":[TD([[makeQuery(id+"F0.imprint","IMPRINT",EDGE,{"disambiguationData":[TD([[subQ6,-1.0]])],"derivedFrom":subQ5}),1.0]])]});}
            var Q32;
            {var subQ1=sQuery(id+"F0.wireOp",EDGE,"E1");var subQ8=sQuery(id+"F0.wireOp",EDGE,"E49");var subQ11=makeQuery(id+"F0.imprint","INTERSECT",VERTEX,{"disambiguationData":[OD(1.0)],"derivedFrom":[subQ1,subQ8]});Q32=makeQuery(id+"F0.imprint","IMPRINT",FACE,{"disambiguationData":[TD([[makeQuery(id+"F0.imprint","IMPRINT",EDGE,{"disambiguationData":[TD([[subQ11,-1.0]])],"derivedFrom":subQ1}),1.0]])]});}
            var Q33;
            {var subQ0=sQuery(id+"F0.wireOp",EDGE,"E45");var subQ1=sQuery(id+"F0.wireOp",EDGE,"E1");var subQ2=makeQuery(id+"F0.imprint","INTERSECT",VERTEX,{"derivedFrom":[subQ1,subQ0]});Q33=makeQuery(id+"F0.imprint","IMPRINT",FACE,{"disambiguationData":[TD([[makeQuery(id+"F0.imprint","IMPRINT",EDGE,{"disambiguationData":[TD([[subQ2,-1.0]])],"derivedFrom":subQ1}),1.0]])]});}
            var Q34;
            {var subQ0=sQuery(id+"F0.wireOp",EDGE,"E3");var subQ1=sQuery(id+"F0.wireOp",EDGE,"E0.bottom");var subQ2=makeQuery(id+"F0.imprint","INTERSECT",VERTEX,{"derivedFrom":[subQ1,subQ0]});Q34=makeQuery(id+"F0.imprint","IMPRINT",FACE,{"disambiguationData":[TD([[makeQuery(id+"F0.imprint","IMPRINT",EDGE,{"disambiguationData":[TD([[subQ2,-1.0]])],"derivedFrom":subQ1}),-1.0]])]});}
            var Q35;
            {var subQ6=sQuery(id+"F0.wireOp",EDGE,"E60");var subQ12=sQuery(id+"F0.wireOp",EDGE,"E66.bottom");var subQ13=makeQuery(id+"F0.imprint","INTERSECT",VERTEX,{"derivedFrom":[subQ6,subQ12]});Q35=makeQuery(id+"F0.imprint","IMPRINT",FACE,{"disambiguationData":[TD([[makeQuery(id+"F0.imprint","IMPRINT",EDGE,{"disambiguationData":[TD([[subQ13,-1.0]])],"derivedFrom":subQ6}),1.0]])]});}
            var Q36;
            {var subQ1=sQuery(id+"F0.wireOp",EDGE,"E0.top");var subQ7=sQuery(id+"F0.wireOp",EDGE,"E3");var subQ8=makeQuery(id+"F0.imprint","INTERSECT",VERTEX,{"derivedFrom":[subQ1,subQ7]});Q36=makeQuery(id+"F0.imprint","IMPRINT",FACE,{"disambiguationData":[TD([[makeQuery(id+"F0.imprint","IMPRINT",EDGE,{"disambiguationData":[TD([[subQ8,-1.0]])],"derivedFrom":subQ1}),1.0]])]});}
            var Q37;
            {var subQ1=sQuery(id+"F0.wireOp",EDGE,"E0.top");var subQ5=sQuery(id+"F0.wireOp",EDGE,"E12");var subQ6=makeQuery(id+"F0.imprint","INTERSECT",VERTEX,{"derivedFrom":[subQ1,subQ5]});Q37=makeQuery(id+"F0.imprint","IMPRINT",FACE,{"disambiguationData":[TD([[makeQuery(id+"F0.imprint","IMPRINT",EDGE,{"disambiguationData":[TD([[subQ6,1.0]])],"derivedFrom":subQ1}),1.0]])]});}
            var Q38;
            {var subQ0=sQuery(id+"F0.wireOp",EDGE,"E38");var subQ1=sQuery(id+"F0.wireOp",EDGE,"E1");var subQ2=makeQuery(id+"F0.imprint","INTERSECT",VERTEX,{"derivedFrom":[subQ1,subQ0]});Q38=makeQuery(id+"F0.imprint","IMPRINT",FACE,{"disambiguationData":[TD([[makeQuery(id+"F0.imprint","IMPRINT",EDGE,{"disambiguationData":[TD([[subQ2,-1.0]])],"derivedFrom":subQ1}),1.0]])]});}
            var Q39;
            {var subQ1=sQuery(id+"F0.wireOp",EDGE,"E0.top");var subQ5=sQuery(id+"F0.wireOp",EDGE,"E44");var subQ6=makeQuery(id+"F0.imprint","INTERSECT",VERTEX,{"derivedFrom":[subQ1,subQ5]});Q39=makeQuery(id+"F0.imprint","IMPRINT",FACE,{"disambiguationData":[TD([[makeQuery(id+"F0.imprint","IMPRINT",EDGE,{"disambiguationData":[TD([[subQ6,1.0]])],"derivedFrom":subQ1}),1.0]])]});}
            var Q40;
            {var subQ0=sQuery(id+"F0.wireOp",EDGE,"E6");var subQ1=sQuery(id+"F0.wireOp",EDGE,"E1");var subQ2=makeQuery(id+"F0.imprint","INTERSECT",VERTEX,{"derivedFrom":[subQ1,subQ0]});Q40=makeQuery(id+"F0.imprint","IMPRINT",FACE,{"disambiguationData":[TD([[makeQuery(id+"F0.imprint","IMPRINT",EDGE,{"disambiguationData":[TD([[subQ2,-1.0]])],"derivedFrom":subQ1}),1.0]])]});}
            var Q41;
            {var subQ0=sQuery(id+"F0.wireOp",EDGE,"E35");var subQ1=sQuery(id+"F0.wireOp",EDGE,"E0.bottom");var subQ2=makeQuery(id+"F0.imprint","INTERSECT",VERTEX,{"derivedFrom":[subQ1,subQ0]});Q41=makeQuery(id+"F0.imprint","IMPRINT",FACE,{"disambiguationData":[TD([[makeQuery(id+"F0.imprint","IMPRINT",EDGE,{"disambiguationData":[TD([[subQ2,-1.0]])],"derivedFrom":subQ1}),-1.0]])]});}
            var Q42;
            {var subQ0=sQuery(id+"F0.wireOp",EDGE,"E27");var subQ1=sQuery(id+"F0.wireOp",EDGE,"E0.bottom");var subQ2=makeQuery(id+"F0.imprint","INTERSECT",VERTEX,{"derivedFrom":[subQ1,subQ0]});Q42=makeQuery(id+"F0.imprint","IMPRINT",FACE,{"disambiguationData":[TD([[makeQuery(id+"F0.imprint","IMPRINT",EDGE,{"disambiguationData":[TD([[subQ2,-1.0]])],"derivedFrom":subQ1}),-1.0]])]});}
            var Q43;
            {var subQ0=sQuery(id+"F0.wireOp",EDGE,"E28");var subQ1=sQuery(id+"F0.wireOp",EDGE,"E0.top");var subQ2=makeQuery(id+"F0.imprint","INTERSECT",VERTEX,{"derivedFrom":[subQ1,subQ0]});Q43=makeQuery(id+"F0.imprint","IMPRINT",FACE,{"disambiguationData":[TD([[makeQuery(id+"F0.imprint","IMPRINT",EDGE,{"disambiguationData":[TD([[subQ2,1.0]])],"derivedFrom":subQ1}),1.0]])]});}
            var Q44;
            {var subQ3=sQuery(id+"F0.wireOp",EDGE,"E12");var subQ5=sQuery(id+"F0.wireOp",EDGE,"E0.top");var subQ6=makeQuery(id+"F0.imprint","INTERSECT",VERTEX,{"derivedFrom":[subQ5,subQ3]});Q44=makeQuery(id+"F0.imprint","IMPRINT",FACE,{"disambiguationData":[TD([[makeQuery(id+"F0.imprint","IMPRINT",EDGE,{"disambiguationData":[TD([[subQ6,-1.0]])],"derivedFrom":subQ5}),1.0]])]});}
            var Q45;
            {var subQ5=sQuery(id+"F0.wireOp",EDGE,"E0.left");var subQ7=sQuery(id+"F0.wireOp",EDGE,"E1");var subQ8=makeQuery(id+"F0.imprint","INTERSECT",VERTEX,{"derivedFrom":[subQ5,subQ7]});Q45=makeQuery(id+"F0.imprint","IMPRINT",FACE,{"disambiguationData":[TD([[makeQuery(id+"F0.imprint","IMPRINT",EDGE,{"disambiguationData":[TD([[subQ8,1.0]])],"derivedFrom":subQ5}),1.0]])]});}
            var Q46;
            {var subQ3=sQuery(id+"F0.wireOp",EDGE,"E28");var subQ5=sQuery(id+"F0.wireOp",EDGE,"E0.top");var subQ6=makeQuery(id+"F0.imprint","INTERSECT",VERTEX,{"derivedFrom":[subQ5,subQ3]});Q46=makeQuery(id+"F0.imprint","IMPRINT",FACE,{"disambiguationData":[TD([[makeQuery(id+"F0.imprint","IMPRINT",EDGE,{"disambiguationData":[TD([[subQ6,-1.0]])],"derivedFrom":subQ5}),1.0]])]});}
            var Q47;
            {var subQ0=sQuery(id+"F0.wireOp",EDGE,"E66.right");Q47=makeQuery(id+"F0.imprint","IMPRINT",FACE,{"disambiguationData":[TD([[makeQuery(id+"F0.imprint","IMPRINT",EDGE,{"derivedFrom":subQ0}),-1.0]])]});}
            var Q48;
            {var subQ1=sQuery(id+"F0.wireOp",EDGE,"E1");var subQ8=sQuery(id+"F0.wireOp",EDGE,"E25");var subQ11=makeQuery(id+"F0.imprint","INTERSECT",VERTEX,{"disambiguationData":[OD(1.0)],"derivedFrom":[subQ1,subQ8]});Q48=makeQuery(id+"F0.imprint","IMPRINT",FACE,{"disambiguationData":[TD([[makeQuery(id+"F0.imprint","IMPRINT",EDGE,{"disambiguationData":[TD([[subQ11,-1.0]])],"derivedFrom":subQ1}),1.0]])]});}
            var Q49;
            {var subQ1=sQuery(id+"F0.wireOp",EDGE,"E0.top");var subQ7=sQuery(id+"F0.wireOp",EDGE,"E51");var subQ9=makeQuery(id+"F0.imprint","INTERSECT",VERTEX,{"derivedFrom":[subQ1,subQ7]});Q49=makeQuery(id+"F0.imprint","IMPRINT",FACE,{"disambiguationData":[TD([[makeQuery(id+"F0.imprint","IMPRINT",EDGE,{"disambiguationData":[TD([[subQ9,-1.0]])],"derivedFrom":subQ1}),1.0]])]});}
            var Q50;
            {var subQ1=sQuery(id+"F0.wireOp",EDGE,"E0.top");var subQ5=sQuery(id+"F0.wireOp",EDGE,"E19");var subQ6=makeQuery(id+"F0.imprint","INTERSECT",VERTEX,{"derivedFrom":[subQ1,subQ5]});Q50=makeQuery(id+"F0.imprint","IMPRINT",FACE,{"disambiguationData":[TD([[makeQuery(id+"F0.imprint","IMPRINT",EDGE,{"disambiguationData":[TD([[subQ6,-1.0]])],"derivedFrom":subQ1}),1.0]])]});}
            var Q51;
            {var subQ0=sQuery(id+"F0.wireOp",EDGE,"E19");var subQ1=sQuery(id+"F0.wireOp",EDGE,"E0.bottom");var subQ2=makeQuery(id+"F0.imprint","INTERSECT",VERTEX,{"derivedFrom":[subQ1,subQ0]});Q51=makeQuery(id+"F0.imprint","IMPRINT",FACE,{"disambiguationData":[TD([[makeQuery(id+"F0.imprint","IMPRINT",EDGE,{"disambiguationData":[TD([[subQ2,1.0]])],"derivedFrom":subQ1}),-1.0]])]});}
            var Q52;
            {var subQ0=sQuery(id+"F0.wireOp",EDGE,"E51");var subQ1=sQuery(id+"F0.wireOp",EDGE,"E0.bottom");var subQ2=makeQuery(id+"F0.imprint","INTERSECT",VERTEX,{"derivedFrom":[subQ1,subQ0]});Q52=makeQuery(id+"F0.imprint","IMPRINT",FACE,{"disambiguationData":[TD([[makeQuery(id+"F0.imprint","IMPRINT",EDGE,{"disambiguationData":[TD([[subQ2,1.0]])],"derivedFrom":subQ1}),-1.0]])]});}
            var Q53;
            {var subQ1=sQuery(id+"F0.wireOp",EDGE,"E0.top");var subQ5=sQuery(id+"F0.wireOp",EDGE,"E30");var subQ6=makeQuery(id+"F0.imprint","INTERSECT",VERTEX,{"derivedFrom":[subQ1,subQ5]});Q53=makeQuery(id+"F0.imprint","IMPRINT",FACE,{"disambiguationData":[TD([[makeQuery(id+"F0.imprint","IMPRINT",EDGE,{"disambiguationData":[TD([[subQ6,-1.0]])],"derivedFrom":subQ1}),1.0]])]});}
            var Q54;
            {var subQ3=sQuery(id+"F0.wireOp",EDGE,"E66.bottom");var subQ6=sQuery(id+"F0.wireOp",EDGE,"E60");var subQ13=makeQuery(id+"F0.imprint","INTERSECT",VERTEX,{"derivedFrom":[subQ6,subQ3]});Q54=makeQuery(id+"F0.imprint","IMPRINT",FACE,{"disambiguationData":[TD([[makeQuery(id+"F0.imprint","IMPRINT",EDGE,{"disambiguationData":[TD([[subQ13,-1.0]])],"derivedFrom":subQ6}),-1.0]])]});}
            var Q55;
            {var subQ0=sQuery(id+"F0.wireOp",EDGE,"E30");var subQ1=sQuery(id+"F0.wireOp",EDGE,"E1");var subQ2=makeQuery(id+"F0.imprint","INTERSECT",VERTEX,{"derivedFrom":[subQ1,subQ0]});Q55=makeQuery(id+"F0.imprint","IMPRINT",FACE,{"disambiguationData":[TD([[makeQuery(id+"F0.imprint","IMPRINT",EDGE,{"disambiguationData":[TD([[subQ2,-1.0]])],"derivedFrom":subQ1}),1.0]])]});}
            var Q56;
            {var subQ1=sQuery(id+"F0.wireOp",EDGE,"E1");var subQ8=sQuery(id+"F0.wireOp",EDGE,"E57");var subQ11=makeQuery(id+"F0.imprint","INTERSECT",VERTEX,{"disambiguationData":[OD(1.0)],"derivedFrom":[subQ1,subQ8]});Q56=makeQuery(id+"F0.imprint","IMPRINT",FACE,{"disambiguationData":[TD([[makeQuery(id+"F0.imprint","IMPRINT",EDGE,{"disambiguationData":[TD([[subQ11,-1.0]])],"derivedFrom":subQ1}),1.0]])]});}
            var Q57;
            {var subQ0=sQuery(id+"F0.wireOp",EDGE,"E36");var subQ1=sQuery(id+"F0.wireOp",EDGE,"E0.bottom");var subQ2=makeQuery(id+"F0.imprint","INTERSECT",VERTEX,{"derivedFrom":[subQ1,subQ0]});Q57=makeQuery(id+"F0.imprint","IMPRINT",FACE,{"disambiguationData":[TD([[makeQuery(id+"F0.imprint","IMPRINT",EDGE,{"disambiguationData":[TD([[subQ2,-1.0]])],"derivedFrom":subQ1}),-1.0]])]});}
            var Q58;
            {var subQ0=sQuery(id+"F0.wireOp",EDGE,"E4");var subQ1=sQuery(id+"F0.wireOp",EDGE,"E0.bottom");var subQ2=makeQuery(id+"F0.imprint","INTERSECT",VERTEX,{"derivedFrom":[subQ1,subQ0]});Q58=makeQuery(id+"F0.imprint","IMPRINT",FACE,{"disambiguationData":[TD([[makeQuery(id+"F0.imprint","IMPRINT",EDGE,{"disambiguationData":[TD([[subQ2,-1.0]])],"derivedFrom":subQ1}),-1.0]])]});}
            var Q59;
            {var subQ0=sQuery(id+"F0.wireOp",EDGE,"E0.left");var subQ1=sQuery(id+"F0.wireOp",EDGE,"E0.bottom");var subQ2=makeQuery(id+"F0.imprint","INTERSECT",VERTEX,{"derivedFrom":[subQ1,subQ0]});Q59=makeQuery(id+"F0.imprint","IMPRINT",FACE,{"disambiguationData":[TD([[makeQuery(id+"F0.imprint","IMPRINT",EDGE,{"disambiguationData":[TD([[subQ2,-1.0]])],"derivedFrom":subQ1}),-1.0]])]});}
            var Q60;
            {var subQ0=sQuery(id+"F0.wireOp",EDGE,"E21");var subQ1=sQuery(id+"F0.wireOp",EDGE,"E1");var subQ2=makeQuery(id+"F0.imprint","INTERSECT",VERTEX,{"derivedFrom":[subQ1,subQ0]});Q60=makeQuery(id+"F0.imprint","IMPRINT",FACE,{"disambiguationData":[TD([[makeQuery(id+"F0.imprint","IMPRINT",EDGE,{"disambiguationData":[TD([[subQ2,-1.0]])],"derivedFrom":subQ1}),1.0]])]});}
            var Q61;
            {var subQ1=sQuery(id+"F0.wireOp",EDGE,"E0.top");var subQ5=sQuery(id+"F0.wireOp",EDGE,"E52");var subQ6=makeQuery(id+"F0.imprint","INTERSECT",VERTEX,{"derivedFrom":[subQ1,subQ5]});Q61=makeQuery(id+"F0.imprint","IMPRINT",FACE,{"disambiguationData":[TD([[makeQuery(id+"F0.imprint","IMPRINT",EDGE,{"disambiguationData":[TD([[subQ6,1.0]])],"derivedFrom":subQ1}),1.0]])]});}
            var Q62;
            {var subQ0=sQuery(id+"F0.wireOp",EDGE,"E20");var subQ1=sQuery(id+"F0.wireOp",EDGE,"E0.bottom");var subQ2=makeQuery(id+"F0.imprint","INTERSECT",VERTEX,{"derivedFrom":[subQ1,subQ0]});Q62=makeQuery(id+"F0.imprint","IMPRINT",FACE,{"disambiguationData":[TD([[makeQuery(id+"F0.imprint","IMPRINT",EDGE,{"disambiguationData":[TD([[subQ2,1.0]])],"derivedFrom":subQ1}),-1.0]])]});}
            var Q63;
            {var subQ0=sQuery(id+"F0.wireOp",EDGE,"E52");var subQ1=sQuery(id+"F0.wireOp",EDGE,"E0.bottom");var subQ2=makeQuery(id+"F0.imprint","INTERSECT",VERTEX,{"derivedFrom":[subQ1,subQ0]});Q63=makeQuery(id+"F0.imprint","IMPRINT",FACE,{"disambiguationData":[TD([[makeQuery(id+"F0.imprint","IMPRINT",EDGE,{"disambiguationData":[TD([[subQ2,1.0]])],"derivedFrom":subQ1}),-1.0]])]});}
            var Q64;
            {var subQ3=sQuery(id+"F0.wireOp",EDGE,"E0.right");var subQ5=sQuery(id+"F0.wireOp",EDGE,"E1");var subQ6=makeQuery(id+"F0.imprint","INTERSECT",VERTEX,{"derivedFrom":[subQ5,subQ3]});Q64=makeQuery(id+"F0.imprint","IMPRINT",FACE,{"disambiguationData":[TD([[makeQuery(id+"F0.imprint","IMPRINT",EDGE,{"disambiguationData":[TD([[subQ6,1.0]])],"derivedFrom":subQ5}),1.0]])]});}
            var Q65;
            {var subQ1=sQuery(id+"F0.wireOp",EDGE,"E0.top");var subQ5=sQuery(id+"F0.wireOp",EDGE,"E20");var subQ6=makeQuery(id+"F0.imprint","INTERSECT",VERTEX,{"derivedFrom":[subQ1,subQ5]});Q65=makeQuery(id+"F0.imprint","IMPRINT",FACE,{"disambiguationData":[TD([[makeQuery(id+"F0.imprint","IMPRINT",EDGE,{"disambiguationData":[TD([[subQ6,1.0]])],"derivedFrom":subQ1}),1.0]])]});}
            var Q66;
            {var subQ0=sQuery(id+"F0.wireOp",EDGE,"E53");var subQ1=sQuery(id+"F0.wireOp",EDGE,"E1");var subQ2=makeQuery(id+"F0.imprint","INTERSECT",VERTEX,{"derivedFrom":[subQ1,subQ0]});Q66=makeQuery(id+"F0.imprint","IMPRINT",FACE,{"disambiguationData":[TD([[makeQuery(id+"F0.imprint","IMPRINT",EDGE,{"disambiguationData":[TD([[subQ2,-1.0]])],"derivedFrom":subQ1}),1.0]])]});}
            var Q67;
            {var subQ0=sQuery(id+"F0.wireOp",EDGE,"E43");var subQ1=sQuery(id+"F0.wireOp",EDGE,"E0.bottom");var subQ2=makeQuery(id+"F0.imprint","INTERSECT",VERTEX,{"derivedFrom":[subQ1,subQ0]});Q67=makeQuery(id+"F0.imprint","IMPRINT",FACE,{"disambiguationData":[TD([[makeQuery(id+"F0.imprint","IMPRINT",EDGE,{"disambiguationData":[TD([[subQ2,1.0]])],"derivedFrom":subQ1}),-1.0]])]});}
            var Q68;
            {var subQ0=sQuery(id+"F0.wireOp",EDGE,"E11");var subQ1=sQuery(id+"F0.wireOp",EDGE,"E0.bottom");var subQ2=makeQuery(id+"F0.imprint","INTERSECT",VERTEX,{"derivedFrom":[subQ1,subQ0]});Q68=makeQuery(id+"F0.imprint","IMPRINT",FACE,{"disambiguationData":[TD([[makeQuery(id+"F0.imprint","IMPRINT",EDGE,{"disambiguationData":[TD([[subQ2,1.0]])],"derivedFrom":subQ1}),-1.0]])]});}
            var Q69;
            {var subQ7=sQuery(id+"F0.wireOp",EDGE,"E58");var subQ9=sQuery(id+"F0.wireOp",EDGE,"E1");var subQ10=makeQuery(id+"F0.imprint","INTERSECT",VERTEX,{"disambiguationData":[OD(1.0)],"derivedFrom":[subQ9,subQ7]});Q69=makeQuery(id+"F0.imprint","IMPRINT",FACE,{"disambiguationData":[TD([[makeQuery(id+"F0.imprint","IMPRINT",EDGE,{"disambiguationData":[TD([[subQ10,-1.0]])],"derivedFrom":subQ9}),1.0]])]});}
            var Q70;
            {var subQ1=sQuery(id+"F0.wireOp",EDGE,"E0.top");var subQ5=sQuery(id+"F0.wireOp",EDGE,"E27");var subQ6=makeQuery(id+"F0.imprint","INTERSECT",VERTEX,{"derivedFrom":[subQ1,subQ5]});Q70=makeQuery(id+"F0.imprint","IMPRINT",FACE,{"disambiguationData":[TD([[makeQuery(id+"F0.imprint","IMPRINT",EDGE,{"disambiguationData":[TD([[subQ6,-1.0]])],"derivedFrom":subQ1}),1.0]])]});}
            var Q71;
            {var subQ1=sQuery(id+"F0.wireOp",EDGE,"E1");var subQ7=sQuery(id+"F0.wireOp",EDGE,"E0.right");var subQ8=makeQuery(id+"F0.imprint","INTERSECT",VERTEX,{"derivedFrom":[subQ1,subQ7]});Q71=makeQuery(id+"F0.imprint","IMPRINT",FACE,{"disambiguationData":[TD([[makeQuery(id+"F0.imprint","IMPRINT",EDGE,{"disambiguationData":[TD([[subQ8,1.0]])],"derivedFrom":subQ1}),-1.0]])]});}
            var Q72;
            {var subQ1=sQuery(id+"F0.wireOp",EDGE,"E1");var subQ8=sQuery(id+"F0.wireOp",EDGE,"E33");var subQ11=makeQuery(id+"F0.imprint","INTERSECT",VERTEX,{"disambiguationData":[OD(1.0)],"derivedFrom":[subQ1,subQ8]});Q72=makeQuery(id+"F0.imprint","IMPRINT",FACE,{"disambiguationData":[TD([[makeQuery(id+"F0.imprint","IMPRINT",EDGE,{"disambiguationData":[TD([[subQ11,-1.0]])],"derivedFrom":subQ1}),1.0]])]});}
            var Q73;
            {var subQ0=sQuery(id+"F0.wireOp",EDGE,"E12");var subQ1=sQuery(id+"F0.wireOp",EDGE,"E0.bottom");var subQ2=makeQuery(id+"F0.imprint","INTERSECT",VERTEX,{"derivedFrom":[subQ1,subQ0]});Q73=makeQuery(id+"F0.imprint","IMPRINT",FACE,{"disambiguationData":[TD([[makeQuery(id+"F0.imprint","IMPRINT",EDGE,{"disambiguationData":[TD([[subQ2,-1.0]])],"derivedFrom":subQ1}),-1.0]])]});}
            var Q74;
            {var subQ0=sQuery(id+"F0.wireOp",EDGE,"E44");var subQ1=sQuery(id+"F0.wireOp",EDGE,"E0.bottom");var subQ2=makeQuery(id+"F0.imprint","INTERSECT",VERTEX,{"derivedFrom":[subQ1,subQ0]});Q74=makeQuery(id+"F0.imprint","IMPRINT",FACE,{"disambiguationData":[TD([[makeQuery(id+"F0.imprint","IMPRINT",EDGE,{"disambiguationData":[TD([[subQ2,-1.0]])],"derivedFrom":subQ1}),-1.0]])]});}
            var Q75;
            {var subQ0=sQuery(id+"F0.wireOp",EDGE,"E43");var subQ1=sQuery(id+"F0.wireOp",EDGE,"E0.bottom");var subQ2=makeQuery(id+"F0.imprint","INTERSECT",VERTEX,{"derivedFrom":[subQ1,subQ0]});Q75=makeQuery(id+"F0.imprint","IMPRINT",FACE,{"disambiguationData":[TD([[makeQuery(id+"F0.imprint","IMPRINT",EDGE,{"disambiguationData":[TD([[subQ2,-1.0]])],"derivedFrom":subQ1}),-1.0]])]});}
            var Q76;
            {var subQ0=sQuery(id+"F0.wireOp",EDGE,"E11");var subQ1=sQuery(id+"F0.wireOp",EDGE,"E0.bottom");var subQ2=makeQuery(id+"F0.imprint","INTERSECT",VERTEX,{"derivedFrom":[subQ1,subQ0]});Q76=makeQuery(id+"F0.imprint","IMPRINT",FACE,{"disambiguationData":[TD([[makeQuery(id+"F0.imprint","IMPRINT",EDGE,{"disambiguationData":[TD([[subQ2,-1.0]])],"derivedFrom":subQ1}),-1.0]])]});}
            var Q77;
            {var subQ7=sQuery(id+"F0.wireOp",EDGE,"E26");var subQ9=sQuery(id+"F0.wireOp",EDGE,"E1");var subQ10=makeQuery(id+"F0.imprint","INTERSECT",VERTEX,{"disambiguationData":[OD(1.0)],"derivedFrom":[subQ9,subQ7]});Q77=makeQuery(id+"F0.imprint","IMPRINT",FACE,{"disambiguationData":[TD([[makeQuery(id+"F0.imprint","IMPRINT",EDGE,{"disambiguationData":[TD([[subQ10,-1.0]])],"derivedFrom":subQ9}),1.0]])]});}
            var Q78;
            {var subQ3=sQuery(id+"F0.wireOp",EDGE,"E52");var subQ7=sQuery(id+"F0.wireOp",EDGE,"E0.top");var subQ8=makeQuery(id+"F0.imprint","INTERSECT",VERTEX,{"derivedFrom":[subQ7,subQ3]});Q78=makeQuery(id+"F0.imprint","IMPRINT",FACE,{"disambiguationData":[TD([[makeQuery(id+"F0.imprint","IMPRINT",EDGE,{"disambiguationData":[TD([[subQ8,-1.0]])],"derivedFrom":subQ7}),1.0]])]});}
            var Q79;
            {var subQ3=sQuery(id+"F0.wireOp",EDGE,"E20");var subQ5=sQuery(id+"F0.wireOp",EDGE,"E0.top");var subQ6=makeQuery(id+"F0.imprint","INTERSECT",VERTEX,{"derivedFrom":[subQ5,subQ3]});Q79=makeQuery(id+"F0.imprint","IMPRINT",FACE,{"disambiguationData":[TD([[makeQuery(id+"F0.imprint","IMPRINT",EDGE,{"disambiguationData":[TD([[subQ6,-1.0]])],"derivedFrom":subQ5}),1.0]])]});}
            var Q80;
            {var subQ0=sQuery(id+"F0.wireOp",EDGE,"E27");var subQ1=sQuery(id+"F0.wireOp",EDGE,"E0.bottom");var subQ2=makeQuery(id+"F0.imprint","INTERSECT",VERTEX,{"derivedFrom":[subQ1,subQ0]});Q80=makeQuery(id+"F0.imprint","IMPRINT",FACE,{"disambiguationData":[TD([[makeQuery(id+"F0.imprint","IMPRINT",EDGE,{"disambiguationData":[TD([[subQ2,1.0]])],"derivedFrom":subQ1}),-1.0]])]});}
            var Q81;
            {var subQ0=sQuery(id+"F0.wireOp",EDGE,"E44");var subQ1=sQuery(id+"F0.wireOp",EDGE,"E0.bottom");var subQ2=makeQuery(id+"F0.imprint","INTERSECT",VERTEX,{"derivedFrom":[subQ1,subQ0]});Q81=makeQuery(id+"F0.imprint","IMPRINT",FACE,{"disambiguationData":[TD([[makeQuery(id+"F0.imprint","IMPRINT",EDGE,{"disambiguationData":[TD([[subQ2,1.0]])],"derivedFrom":subQ1}),-1.0]])]});}
            var Q82;
            {var subQ0=sQuery(id+"F0.wireOp",EDGE,"E12");var subQ1=sQuery(id+"F0.wireOp",EDGE,"E0.bottom");var subQ2=makeQuery(id+"F0.imprint","INTERSECT",VERTEX,{"derivedFrom":[subQ1,subQ0]});Q82=makeQuery(id+"F0.imprint","IMPRINT",FACE,{"disambiguationData":[TD([[makeQuery(id+"F0.imprint","IMPRINT",EDGE,{"disambiguationData":[TD([[subQ2,1.0]])],"derivedFrom":subQ1}),-1.0]])]});}
            var Q83;
            {var subQ0=sQuery(id+"F0.wireOp",EDGE,"E59");var subQ1=sQuery(id+"F0.wireOp",EDGE,"E0.bottom");var subQ2=makeQuery(id+"F0.imprint","INTERSECT",VERTEX,{"derivedFrom":[subQ1,subQ0]});Q83=makeQuery(id+"F0.imprint","IMPRINT",FACE,{"disambiguationData":[TD([[makeQuery(id+"F0.imprint","IMPRINT",EDGE,{"disambiguationData":[TD([[subQ2,1.0]])],"derivedFrom":subQ1}),-1.0]])]});}
            var Q84;
            {var subQ1=sQuery(id+"F0.wireOp",EDGE,"E0.top");var subQ5=sQuery(id+"F0.wireOp",EDGE,"E36");var subQ6=makeQuery(id+"F0.imprint","INTERSECT",VERTEX,{"derivedFrom":[subQ1,subQ5]});Q84=makeQuery(id+"F0.imprint","IMPRINT",FACE,{"disambiguationData":[TD([[makeQuery(id+"F0.imprint","IMPRINT",EDGE,{"disambiguationData":[TD([[subQ6,1.0]])],"derivedFrom":subQ1}),1.0]])]});}
            var Q85;
            {var subQ3=sQuery(id+"F0.wireOp",EDGE,"E22");var subQ5=sQuery(id+"F0.wireOp",EDGE,"E1");var subQ6=makeQuery(id+"F0.imprint","INTERSECT",VERTEX,{"derivedFrom":[subQ5,subQ3]});Q85=makeQuery(id+"F0.imprint","IMPRINT",FACE,{"disambiguationData":[TD([[makeQuery(id+"F0.imprint","IMPRINT",EDGE,{"disambiguationData":[TD([[subQ6,-1.0]])],"derivedFrom":subQ5}),1.0]])]});}
            var Q86;
            {var subQ1=sQuery(id+"F0.wireOp",EDGE,"E0.top");var subQ5=sQuery(id+"F0.wireOp",EDGE,"E4");var subQ6=makeQuery(id+"F0.imprint","INTERSECT",VERTEX,{"derivedFrom":[subQ1,subQ5]});Q86=makeQuery(id+"F0.imprint","IMPRINT",FACE,{"disambiguationData":[TD([[makeQuery(id+"F0.imprint","IMPRINT",EDGE,{"disambiguationData":[TD([[subQ6,1.0]])],"derivedFrom":subQ1}),1.0]])]});}
            var Q87;
            {var subQ0=sQuery(id+"F0.wireOp",EDGE,"E54");var subQ6=sQuery(id+"F0.wireOp",EDGE,"E0.top");var subQ9=makeQuery(id+"F0.imprint","INTERSECT",VERTEX,{"derivedFrom":[subQ6,subQ0]});Q87=makeQuery(id+"F0.imprint","IMPRINT",FACE,{"disambiguationData":[TD([[makeQuery(id+"F0.imprint","IMPRINT",EDGE,{"disambiguationData":[TD([[subQ9,-1.0]])],"derivedFrom":subQ6}),1.0]])]});}
            var Q88;
            {var subQ1=sQuery(id+"F0.wireOp",EDGE,"E0.top");var subQ5=sQuery(id+"F0.wireOp",EDGE,"E22");var subQ6=makeQuery(id+"F0.imprint","INTERSECT",VERTEX,{"derivedFrom":[subQ1,subQ5]});Q88=makeQuery(id+"F0.imprint","IMPRINT",FACE,{"disambiguationData":[TD([[makeQuery(id+"F0.imprint","IMPRINT",EDGE,{"disambiguationData":[TD([[subQ6,-1.0]])],"derivedFrom":subQ1}),1.0]])]});}
            var Q89;
            {var subQ0=sQuery(id+"F0.wireOp",EDGE,"E37");var subQ1=sQuery(id+"F0.wireOp",EDGE,"E1");var subQ2=makeQuery(id+"F0.imprint","INTERSECT",VERTEX,{"derivedFrom":[subQ1,subQ0]});Q89=makeQuery(id+"F0.imprint","IMPRINT",FACE,{"disambiguationData":[TD([[makeQuery(id+"F0.imprint","IMPRINT",EDGE,{"disambiguationData":[TD([[subQ2,-1.0]])],"derivedFrom":subQ1}),1.0]])]});}
            var Q90;
            {var subQ0=sQuery(id+"F0.wireOp",EDGE,"E5");var subQ1=sQuery(id+"F0.wireOp",EDGE,"E1");var subQ2=makeQuery(id+"F0.imprint","INTERSECT",VERTEX,{"derivedFrom":[subQ1,subQ0]});Q90=makeQuery(id+"F0.imprint","IMPRINT",FACE,{"disambiguationData":[TD([[makeQuery(id+"F0.imprint","IMPRINT",EDGE,{"disambiguationData":[TD([[subQ2,-1.0]])],"derivedFrom":subQ1}),1.0]])]});}
            var Q91;
            {var subQ0=sQuery(id+"F0.wireOp",EDGE,"E54");var subQ1=sQuery(id+"F0.wireOp",EDGE,"E1");var subQ2=makeQuery(id+"F0.imprint","INTERSECT",VERTEX,{"derivedFrom":[subQ1,subQ0]});Q91=makeQuery(id+"F0.imprint","IMPRINT",FACE,{"disambiguationData":[TD([[makeQuery(id+"F0.imprint","IMPRINT",EDGE,{"disambiguationData":[TD([[subQ2,-1.0]])],"derivedFrom":subQ1}),1.0]])]});}
            var Q92;
            {var subQ0=sQuery(id+"F0.wireOp",EDGE,"E29");var subQ1=sQuery(id+"F0.wireOp",EDGE,"E1");var subQ2=makeQuery(id+"F0.imprint","INTERSECT",VERTEX,{"derivedFrom":[subQ1,subQ0]});Q92=makeQuery(id+"F0.imprint","IMPRINT",FACE,{"disambiguationData":[TD([[makeQuery(id+"F0.imprint","IMPRINT",EDGE,{"disambiguationData":[TD([[subQ2,-1.0]])],"derivedFrom":subQ1}),1.0]])]});}
            extrude(context, id + "F1", {"entities" : qUnion([Q0, Q1, Q2, Q3, Q4, Q5, Q6, Q7, Q8, Q9, Q10, Q11, Q12, Q13, Q14, Q15, Q16, Q17, Q18, Q19, Q20, Q21, Q22, Q23, Q24, Q25, Q26, Q27, Q28, Q29, Q30, Q31, Q32, Q33, Q34, Q35, Q36, Q37, Q38, Q39, Q40, Q41, Q42, Q43, Q44, Q45, Q46, Q47, Q48, Q49, Q50, Q51, Q52, Q53, Q54, Q55, Q56, Q57, Q58, Q59, Q60, Q61, Q62, Q63, Q64, Q65, Q66, Q67, Q68, Q69, Q70, Q71, Q72, Q73, Q74, Q75, Q76, Q77, Q78, Q79, Q80, Q81, Q82, Q83, Q84, Q85, Q86, Q87, Q88, Q89, Q90, Q91, Q92]), "depth" : 3.17 * mm, "offsetDistance" : 25.4 * mm});
        }
        {
            var Q0;
            Q0=makeQuery(id+"F1.opExtrude","CAP_FACE",FACE,{"disambiguationData":[OSD([sQuery(id+"F0.wireOp",EDGE,"E0.bottom"),sQuery(id+"F0.wireOp",EDGE,"E0.top"),sQuery(id+"F0.wireOp",EDGE,"E0.left"),sQuery(id+"F0.wireOp",EDGE,"E7.bottom"),sQuery(id+"F0.wireOp",EDGE,"E7.left"),sQuery(id+"F0.wireOp",EDGE,"E7.right"),sQuery(id+"F0.wireOp",EDGE,"E8.bottom"),sQuery(id+"F0.wireOp",EDGE,"E8.left"),sQuery(id+"F0.wireOp",EDGE,"E8.right"),sQuery(id+"F0.wireOp",EDGE,"E9"),sQuery(id+"F0.wireOp",EDGE,"E10"),sQuery(id+"F0.wireOp",EDGE,"E15.bottom"),sQuery(id+"F0.wireOp",EDGE,"E15.left"),sQuery(id+"F0.wireOp",EDGE,"E15.right"),sQuery(id+"F0.wireOp",EDGE,"E16.bottom"),sQuery(id+"F0.wireOp",EDGE,"E16.left"),sQuery(id+"F0.wireOp",EDGE,"E16.right"),sQuery(id+"F0.wireOp",EDGE,"E17"),sQuery(id+"F0.wireOp",EDGE,"E18"),sQuery(id+"F0.wireOp",EDGE,"E23.bottom"),sQuery(id+"F0.wireOp",EDGE,"E23.left"),sQuery(id+"F0.wireOp",EDGE,"E23.right"),sQuery(id+"F0.wireOp",EDGE,"E24.bottom"),sQuery(id+"F0.wireOp",EDGE,"E24.left"),sQuery(id+"F0.wireOp",EDGE,"E24.right"),sQuery(id+"F0.wireOp",EDGE,"E25"),sQuery(id+"F0.wireOp",EDGE,"E26"),sQuery(id+"F0.wireOp",EDGE,"E31.bottom"),sQuery(id+"F0.wireOp",EDGE,"E31.left"),sQuery(id+"F0.wireOp",EDGE,"E31.right"),sQuery(id+"F0.wireOp",EDGE,"E32.bottom"),sQuery(id+"F0.wireOp",EDGE,"E32.left"),sQuery(id+"F0.wireOp",EDGE,"E32.right"),sQuery(id+"F0.wireOp",EDGE,"E33"),sQuery(id+"F0.wireOp",EDGE,"E34"),sQuery(id+"F0.wireOp",EDGE,"E39.bottom"),sQuery(id+"F0.wireOp",EDGE,"E39.left"),sQuery(id+"F0.wireOp",EDGE,"E39.right"),sQuery(id+"F0.wireOp",EDGE,"E40.bottom"),sQuery(id+"F0.wireOp",EDGE,"E40.left"),sQuery(id+"F0.wireOp",EDGE,"E40.right"),sQuery(id+"F0.wireOp",EDGE,"E41"),sQuery(id+"F0.wireOp",EDGE,"E42"),sQuery(id+"F0.wireOp",EDGE,"E47.bottom"),sQuery(id+"F0.wireOp",EDGE,"E47.left"),sQuery(id+"F0.wireOp",EDGE,"E47.right"),sQuery(id+"F0.wireOp",EDGE,"E48.bottom"),sQuery(id+"F0.wireOp",EDGE,"E48.left"),sQuery(id+"F0.wireOp",EDGE,"E48.right"),sQuery(id+"F0.wireOp",EDGE,"E49"),sQuery(id+"F0.wireOp",EDGE,"E50"),sQuery(id+"F0.wireOp",EDGE,"E55.bottom"),sQuery(id+"F0.wireOp",EDGE,"E55.left"),sQuery(id+"F0.wireOp",EDGE,"E55.right"),sQuery(id+"F0.wireOp",EDGE,"E56.bottom"),sQuery(id+"F0.wireOp",EDGE,"E56.left"),sQuery(id+"F0.wireOp",EDGE,"E56.right"),sQuery(id+"F0.wireOp",EDGE,"E57"),sQuery(id+"F0.wireOp",EDGE,"E58"),sQuery(id+"F0.wireOp",EDGE,"E62.bottom"),sQuery(id+"F0.wireOp",EDGE,"E62.left"),sQuery(id+"F0.wireOp",EDGE,"E62.right"),sQuery(id+"F0.wireOp",EDGE,"E63.bottom"),sQuery(id+"F0.wireOp",EDGE,"E63.left"),sQuery(id+"F0.wireOp",EDGE,"E63.right"),sQuery(id+"F0.wireOp",EDGE,"E64"),sQuery(id+"F0.wireOp",EDGE,"E65"),sQuery(id+"F0.wireOp",EDGE,"E66.bottom"),sQuery(id+"F0.wireOp",EDGE,"E66.top"),sQuery(id+"F0.wireOp",EDGE,"E66.right")])],"isStart":true});
            var sketch = newSketch(context, id + "F2", { "sketchPlane" : qUnion([Q0])});
            skLineSegment(sketch, "E67.bottom", {"start": v(-114.3, -15.24) * mm, "end": v(-105.43, -15.24) * mm});
            skLineSegment(sketch, "E67.top", {"start": v(-114.3, 3.81) * mm, "end": v(-105.43, 3.81) * mm});
            skLineSegment(sketch, "E67.left", {"start": v(-114.3, -15.24) * mm, "end": v(-114.3, 3.81) * mm});
            skLineSegment(sketch, "E67.right", {"start": v(-105.43, -15.24) * mm, "end": v(-105.43, 3.81) * mm});
            skSolve(sketch);
        }
        {
            var Q0;
            Q0=makeQuery(id+"F2.imprint","IMPRINT",FACE,{"disambiguationData":[TD([[makeQuery(id+"F2.imprint","IMPRINT",EDGE,{"derivedFrom":sQuery(id+"F2.wireOp",EDGE,"E67.bottom")}),-1.0]])]});
            extrude(context, id + "F3", {"entities" : qUnion([Q0]), "operationType" : NewBodyOperationType.ADD, "depth" : 19.05 * mm, "offsetDistance" : 25.4 * mm});
        }
        {
            var Q0;
            Q0=makeQuery(id+"F1.opExtrude","CAP_FACE",FACE,{"disambiguationData":[OSD([sQuery(id+"F0.wireOp",EDGE,"E0.bottom"),sQuery(id+"F0.wireOp",EDGE,"E0.top"),sQuery(id+"F0.wireOp",EDGE,"E0.left"),sQuery(id+"F0.wireOp",EDGE,"E7.bottom"),sQuery(id+"F0.wireOp",EDGE,"E7.left"),sQuery(id+"F0.wireOp",EDGE,"E7.right"),sQuery(id+"F0.wireOp",EDGE,"E8.bottom"),sQuery(id+"F0.wireOp",EDGE,"E8.left"),sQuery(id+"F0.wireOp",EDGE,"E8.right"),sQuery(id+"F0.wireOp",EDGE,"E9"),sQuery(id+"F0.wireOp",EDGE,"E10"),sQuery(id+"F0.wireOp",EDGE,"E15.bottom"),sQuery(id+"F0.wireOp",EDGE,"E15.left"),sQuery(id+"F0.wireOp",EDGE,"E15.right"),sQuery(id+"F0.wireOp",EDGE,"E16.bottom"),sQuery(id+"F0.wireOp",EDGE,"E16.left"),sQuery(id+"F0.wireOp",EDGE,"E16.right"),sQuery(id+"F0.wireOp",EDGE,"E17"),sQuery(id+"F0.wireOp",EDGE,"E18"),sQuery(id+"F0.wireOp",EDGE,"E23.bottom"),sQuery(id+"F0.wireOp",EDGE,"E23.left"),sQuery(id+"F0.wireOp",EDGE,"E23.right"),sQuery(id+"F0.wireOp",EDGE,"E24.bottom"),sQuery(id+"F0.wireOp",EDGE,"E24.left"),sQuery(id+"F0.wireOp",EDGE,"E24.right"),sQuery(id+"F0.wireOp",EDGE,"E25"),sQuery(id+"F0.wireOp",EDGE,"E26"),sQuery(id+"F0.wireOp",EDGE,"E31.bottom"),sQuery(id+"F0.wireOp",EDGE,"E31.left"),sQuery(id+"F0.wireOp",EDGE,"E31.right"),sQuery(id+"F0.wireOp",EDGE,"E32.bottom"),sQuery(id+"F0.wireOp",EDGE,"E32.left"),sQuery(id+"F0.wireOp",EDGE,"E32.right"),sQuery(id+"F0.wireOp",EDGE,"E33"),sQuery(id+"F0.wireOp",EDGE,"E34"),sQuery(id+"F0.wireOp",EDGE,"E39.bottom"),sQuery(id+"F0.wireOp",EDGE,"E39.left"),sQuery(id+"F0.wireOp",EDGE,"E39.right"),sQuery(id+"F0.wireOp",EDGE,"E40.bottom"),sQuery(id+"F0.wireOp",EDGE,"E40.left"),sQuery(id+"F0.wireOp",EDGE,"E40.right"),sQuery(id+"F0.wireOp",EDGE,"E41"),sQuery(id+"F0.wireOp",EDGE,"E42"),sQuery(id+"F0.wireOp",EDGE,"E47.bottom"),sQuery(id+"F0.wireOp",EDGE,"E47.left"),sQuery(id+"F0.wireOp",EDGE,"E47.right"),sQuery(id+"F0.wireOp",EDGE,"E48.bottom"),sQuery(id+"F0.wireOp",EDGE,"E48.left"),sQuery(id+"F0.wireOp",EDGE,"E48.right"),sQuery(id+"F0.wireOp",EDGE,"E49"),sQuery(id+"F0.wireOp",EDGE,"E50"),sQuery(id+"F0.wireOp",EDGE,"E55.bottom"),sQuery(id+"F0.wireOp",EDGE,"E55.left"),sQuery(id+"F0.wireOp",EDGE,"E55.right"),sQuery(id+"F0.wireOp",EDGE,"E56.bottom"),sQuery(id+"F0.wireOp",EDGE,"E56.left"),sQuery(id+"F0.wireOp",EDGE,"E56.right"),sQuery(id+"F0.wireOp",EDGE,"E57"),sQuery(id+"F0.wireOp",EDGE,"E58"),sQuery(id+"F0.wireOp",EDGE,"E62.bottom"),sQuery(id+"F0.wireOp",EDGE,"E62.left"),sQuery(id+"F0.wireOp",EDGE,"E62.right"),sQuery(id+"F0.wireOp",EDGE,"E63.bottom"),sQuery(id+"F0.wireOp",EDGE,"E63.left"),sQuery(id+"F0.wireOp",EDGE,"E63.right"),sQuery(id+"F0.wireOp",EDGE,"E64"),sQuery(id+"F0.wireOp",EDGE,"E65"),sQuery(id+"F0.wireOp",EDGE,"E66.bottom"),sQuery(id+"F0.wireOp",EDGE,"E66.top"),sQuery(id+"F0.wireOp",EDGE,"E66.right")])],"isStart":true});
            var sketch = newSketch(context, id + "F4", { "sketchPlane" : qUnion([Q0])});
            skLineSegment(sketch, "E68.bottom", {"start": v(95.25, 15.24) * mm, "end": v(85.84, 15.24) * mm});
            skLineSegment(sketch, "E68.top", {"start": v(95.25, -1.73) * mm, "end": v(85.84, -1.73) * mm});
            skLineSegment(sketch, "E68.left", {"start": v(95.25, 15.24) * mm, "end": v(95.25, -1.73) * mm});
            skLineSegment(sketch, "E68.right", {"start": v(85.84, 15.24) * mm, "end": v(85.84, -1.73) * mm});
            skSolve(sketch);
        }
        {
            var Q0;
            Q0 = qSketchRegion(id + "F4", true);
            var Q1;
            Q1=makeQuery(id+"F4.imprint","IMPRINT",FACE,{"disambiguationData":[TD([[makeQuery(id+"F4.imprint","IMPRINT",EDGE,{"derivedFrom":sQuery(id+"F4.wireOp",EDGE,"E68.bottom")}),1.0]])]});
            extrude(context, id + "F5", {"entities" : qUnion([Q0, Q1]), "operationType" : NewBodyOperationType.ADD, "depth" : 19.05 * mm, "offsetDistance" : 25.4 * mm});
        }
    });
